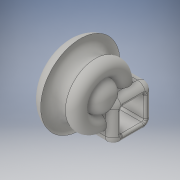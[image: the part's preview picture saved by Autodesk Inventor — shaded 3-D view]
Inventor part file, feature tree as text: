
AUTODESK INVENTOR PART (.ipt)
format: ipt  version: 2016 (Build 200138000, 138)  size: 487,424 bytes
history: native  units: in
note: dims shown in document units (in); Inventor stores cm internally (conversion verified against a paired STEP export)
features: fillet x9, sketch x3, extrude x2, revolve x1
ambient origin geometry x8: Origin, YZ Plane, XZ Plane, XY Plane, X Axis, Y Axis, Z Axis, Center Point
bodies: Solid1 (feature_tree)
feature tree (15):
  revolve  "Revolution1"  [1 undecoded]
  extrude  "Extrusion1"  Depth=1.5in TaperAngle=0.0deg
  fillet  "Fillet1"  Radius=0.3in
  fillet  "Fillet2"  Radius=0.3in
  fillet  "Fillet3"  Radius=0.3in
  extrude  "Extrusion2"  Depth=0.3in
  fillet  "Fillet4"  Radius=0.075in
  fillet  "Fillet5"  Radius=0.075in
  fillet  "Fillet6"  Radius=0.075in
  fillet  "Fillet7"  Radius=0.075in
  fillet  "Fillet8"  Radius=0.075in
  fillet  "Fillet9"  [1 undecoded]
  sketch  "Sketch1"  dims[d0=270.0deg d1=1.75in]
  sketch  "Sketch2"  dims[d2=1.5in d3=1.5in d4=0.0in d5=0.3in d6=0.3in d7=0.3in]
  sketch  "Sketch3"  dims[d8=1.5in d9=0.0in d10=0.3in d11=0.075in d12=0.075in d13=0.075in d14=0.075in d15=0.075in]
note: 2 required parameter values undecoded (feature->parameter linkage not recoverable at this tier; creation-order binding heuristic only, values carry confidence <= 0.55)